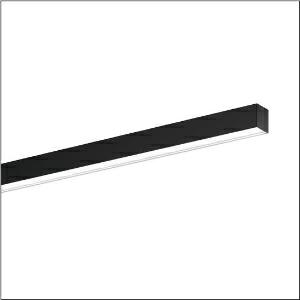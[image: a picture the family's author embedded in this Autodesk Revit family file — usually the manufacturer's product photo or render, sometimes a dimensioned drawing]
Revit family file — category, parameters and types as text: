
# Revit family: silica_r__21_51mx23tat4b_8a74
name_source: partatom
category: Lighting Fixtures
units: mm (PartAtom-declared; Revit-internal decimal feet)

## family parameters
Cut with Voids When Loaded = No
Host = Face
Light Source = No
Part Type = Normal
Room Calculation Point = No
Round Connector Dimension = Use Diameter
Shared = No

## types (1)
- --- (1 x LED, 3230 lm, 32.4 W, 6500K)
    Apparent Load = 32 VA
    CIE Flux Codes = 78 96 99 100 100
    Color Rendering = 80
    Color Temperature = 6500K
    Default Elevation = 1800 mm
    Description = Silica® 21, office luminaire, primary optical cover: prismatic diffuser, of PMMA, CAT 2 (L<= 3000cd/m²), light emission: direct distribution, primary light characteristic: symmetric, installation type: surface-mounted, LED, rated luminous flux: 3.230lm, luminous efficacy: 95lm/W, light colour: 8tw, colour temperature: 2700..6500K, control gear: ECG DALI, with terminal, 3+2-pole, max. 2.5mm², mains connection: 220..240V, AC, 50/60Hz, rated input power: 34W, luminaire housing, of aluminium, jet black (RAL 9005), length: 1.204mm, width: 53mm, height: 53mm, protection rating (complete): IP20, insulation class (complete): insulation class I (protective earthing), certification: CE, permissible operating ambient temperature: 0..+35°C, standard: EN 50419, packaging unit: 1 piece
    Height = 0 mm  [stored 0 ft]
    Lamp = 1 x LED
    Lamp Light Flux = 3230 lm
    Lamp Power = 32.4 W
    Lamp count = 1
    Length = 1204 mm
    Luminous efficacy = 100 lm/W
    Manufacturer = Siteco
    ModVariant = No
    Model = 51MX23TAT4B
    Mounting Place = Ceiling
    Mounting Type = Recessed
    Number of Poles = 1
    OnlyDefault = Yes
    Power Factor = 1
    Product Name = Silica® 21
    Product group = office luminaire | ceiling recessed
    ProductGroupID = 401
    Protection Class = Protection class I
    Protection Degree = IP 20
    RLX_Detail_Level = 1
    RLX_Emergency_Light_Flux = 0 lm
    RLX_Emergency_Type = 0
    RLX_Emergency_Type_DB = No
    RlxData = <blob elided: 20493 chars, md5=1cd937d2>
    Socket = socket
    Standby Power = 0 W
    System Light Flux = 3230 lm
    System Power = 32 W
    Type Comments = individual setting
    Type Image = l_1313584.jpg
    URL = http://relux.com
    VarID = @adj_089187
    Voltage = 0 V
    Weight = 0.00 kg
    Width = 53 mm

note: [stored X ft] marks values corroborated as IEEE doubles in the binary element streams (Revit-internal decimal feet)

## geometry (parser evidence)
native form markers: Blend x4, Sweep x11
no freeform markers — native parametric forms only
